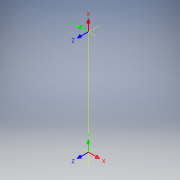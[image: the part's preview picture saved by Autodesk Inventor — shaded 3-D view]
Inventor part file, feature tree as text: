
AUTODESK INVENTOR PART (.ipt)
format: ipt  version: 2019 (Build 230136000, 136)  size: 108,032 bytes
history: native  units: in
note: dims shown in document units (in); Inventor stores cm internally (conversion verified against a paired STEP export)
features: other x19, sketch x2, plane x1
ambient origin geometry x4: Origin, YZ Plane, XZ Plane, XY Plane
feature tree (22):
  parser-record x1  (decoder bookkeeping rows leaked as tree rows — omitted from the tree; the rows remain in map.json)
  other  "d offset"
  other  "theta offset"
  other  "r_offset"
  other  "alpha offset"
  sketch  "Sketch4"  dims[d0=0.0in d1=0.0in d2=0.0in d3=0.0in d4=0.0in d5=0.0in d7=0.0in d8=0.0in d11=1.8898in d12=90.0deg d13=0.0394in d14=0.0394in d15=0.0in d16=0.0in d17=0.0in d18=0.0in d19=0.0in d20=0.0in]
  sketch  "3D Sketch2"
  plane  "Work Plane5"
  other  "UCS2: YZ Plane"
  other  "UCS2: XZ Plane"
  other  "UCS2: XY Plane"
  other  "UCS2: X Axis"
  other  "UCS2: Y Axis"
  other  "UCS2: Z Axis"
  other  "UCS2: Center Point"
  other  "UCS3: YZ Plane"
  other  "UCS3: XZ Plane"
  other  "UCS3: XY Plane"
  other  "UCS3: X Axis"
  other  "UCS3: Y Axis"
  other  "UCS3: Z Axis"
  other  "UCS3: Center Point"
note: 1 file-system path scrubbed to <path> (originals preserved in map.json)
